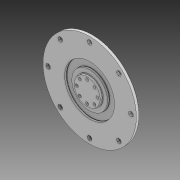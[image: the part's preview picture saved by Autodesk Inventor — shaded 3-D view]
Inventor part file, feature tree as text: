
AUTODESK INVENTOR PART (.ipt)
format: ipt  version: 2020 (Build 240168000, 168)  size: 367,616 bytes
history: native  units: mm
features: sketch x7, extrude x5, revolve x1, chamfer x1
ambient origin geometry x8: Origin, YZ Plane, XZ Plane, XY Plane, X Axis, Y Axis, Z Axis, Center Point
bodies: Solid1 (feature_tree)
feature tree (14):
  extrude  "Extrusion1"  Depth=2.0mm TaperAngle=0.0deg
  sketch  "Sketch2"  dims[d3=400.0mm d4=600.0mm]
  revolve  "Revolution1"  [1 undecoded]
  extrude  "Extrusion2"  Depth=1000.0mm
  extrude  "Extrusion3"  TaperAngle=90.0deg  [1 undecoded]
  extrude  "Extrusion4"  Depth=20.0mm
  extrude  "Extrusion5"  TaperAngle=0.0deg  [1 undecoded]
  chamfer  "Chamfer1"  Distance=80.0mm Angle=360.0deg
  sketch  "Sketch1"  dims[d0=180.0mm d1=2.0mm d2=0.0mm]
  sketch  "Sketch3"  dims[d5=800.0mm d6=1000.0mm]
  sketch  "Sketch4"  dims[d9=0.0mm d14=90.0deg]
  sketch  "Sketch5"  dims[d16=20.0mm d17=5.5mm]
  sketch  "Sketch6"  dims[d18=80.0mm d20=360.0deg d22=0.0mm d23=0.0mm]
  sketch  "Sketch7"  dims[d24=9.5mm d25=80.0mm d27=360.0deg d29=6.0mm d30=0.0mm d33=25.0mm d36=1.5mm d38=5.0mm d39=4.0mm d40=8.7mm d41=4.0mm d43=0.8mm d44=34.9mm d45=47.6mm d46=80.0mm d47=5.5mm d48=80.0mm d50=360.0deg d52=0.0mm d53=0.0mm d54=8.2mm d55=80.0mm d57=360.0deg d59=4.0mm d60=0.0mm d61=1.0mm d62=2.0mm d63=45.0deg d64=0.5mm d66=0.5mm]
note: 3 required parameter values undecoded (feature->parameter linkage not recoverable at this tier; creation-order binding heuristic only, values carry confidence <= 0.55)